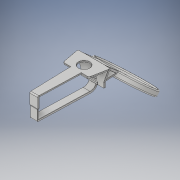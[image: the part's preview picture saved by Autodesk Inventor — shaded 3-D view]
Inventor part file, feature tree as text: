
AUTODESK INVENTOR PART (.ipt)
format: ipt  version: 2017 (Build 210142000, 142)  size: 1,435,136 bytes
history: native  units: mm
features: extrude x10, sketch x10, fillet x9, other x2, plane x1
ambient origin geometry x8: Origin, YZ Plane, XZ Plane, XY Plane, X Axis, Y Axis, Z Axis, Center Point
bodies: Body1 (feature_tree)
feature tree (32):
  extrude  "Extrusion2"  Depth=2.5mm TaperAngle=0.0deg
  extrude  "Extrusion3"  Depth=12.391838mm
  extrude  "Extrusion5"  Depth=28.099801mm
  plane  "Work Plane1"
  extrude  "Extrusion6"  Depth=6.5mm
  extrude  "Extrusion7"  Depth=3.5mm TaperAngle=0.0deg
  extrude  "Extrusion8"  Depth=2.5mm TaperAngle=0.0deg
  extrude  "Extrusion9"  Depth=2.5mm
  extrude  "Extrusion10"  Depth=2.5mm
  extrude  "Extrusion11"  Depth=22.863813mm
  fillet  "Fillet1"  Radius=4.0mm
  fillet  "Fillet3"  Radius=38.0mm
  fillet  "Fillet4"  Radius=10.0mm
  fillet  "Fillet5"  Radius=10.0mm
  fillet  "Fillet6"  Radius=1.4mm
  extrude  "Extrusion13"  Depth=2.0mm
  fillet  "Fillet8"  [1 undecoded]
  fillet  "Fillet9"  Radius=0.45mm
  fillet  "Fillet10"  Radius=2.0mm
  fillet  "Fillet11"  Radius=0.5mm
  sketch  "sketch1 - front_main"  dims[d66=26.0mm d67=12.391838mm]
  other  "Image1"
  sketch  "sketch2 - bottom_front_tab"  dims[d68=26.0mm d69=28.099801mm]
  sketch  "sketch3 - top_tab"  dims[d70=9.0mm d73=6.5mm]
  other  "Image2"
  sketch  "sketch5 - bottom_hinge"  dims[d74=6.5mm d76=3.5mm d77=0.0mm]
  sketch  "sketch6 - hinge_part"  dims[d82=17.0mm d88=2.5mm d89=0.0mm]
  sketch  "sketch7 - drink_arm"  dims[d90=12.789mm d91=0.0mm d92=2.5mm]
  sketch  "sketch8 - support_arm_arc_hole"  dims[d94=4.6mm d95=2.5mm]
  sketch  "sketch9 - cup_holder"  dims[d96=3.5mm d97=0.0mm d98=22.863813mm d99=4.0mm d100=38.0mm d101=0.0mm d106=10.0mm d107=0.0mm d109=10.0mm d110=0.0mm d111=1.4mm]
  sketch  "Sketch13"  dims[d12=2.5mm d13=0.0mm d18=2.5mm d19=0.0mm]
  sketch  "sketch4 - xbox_hole"  dims[d113=0.4mm d118=20.0mm d119=90.0deg d120=0.45mm d121=2.0mm d122=0.5mm d125=3.0mm d126=0.0mm d128=0.45mm d129=0.45mm d130=4.0mm d131=2.0mm]
note: 1 required parameter value undecoded (feature->parameter linkage not recoverable at this tier; creation-order binding heuristic only, values carry confidence <= 0.55)
